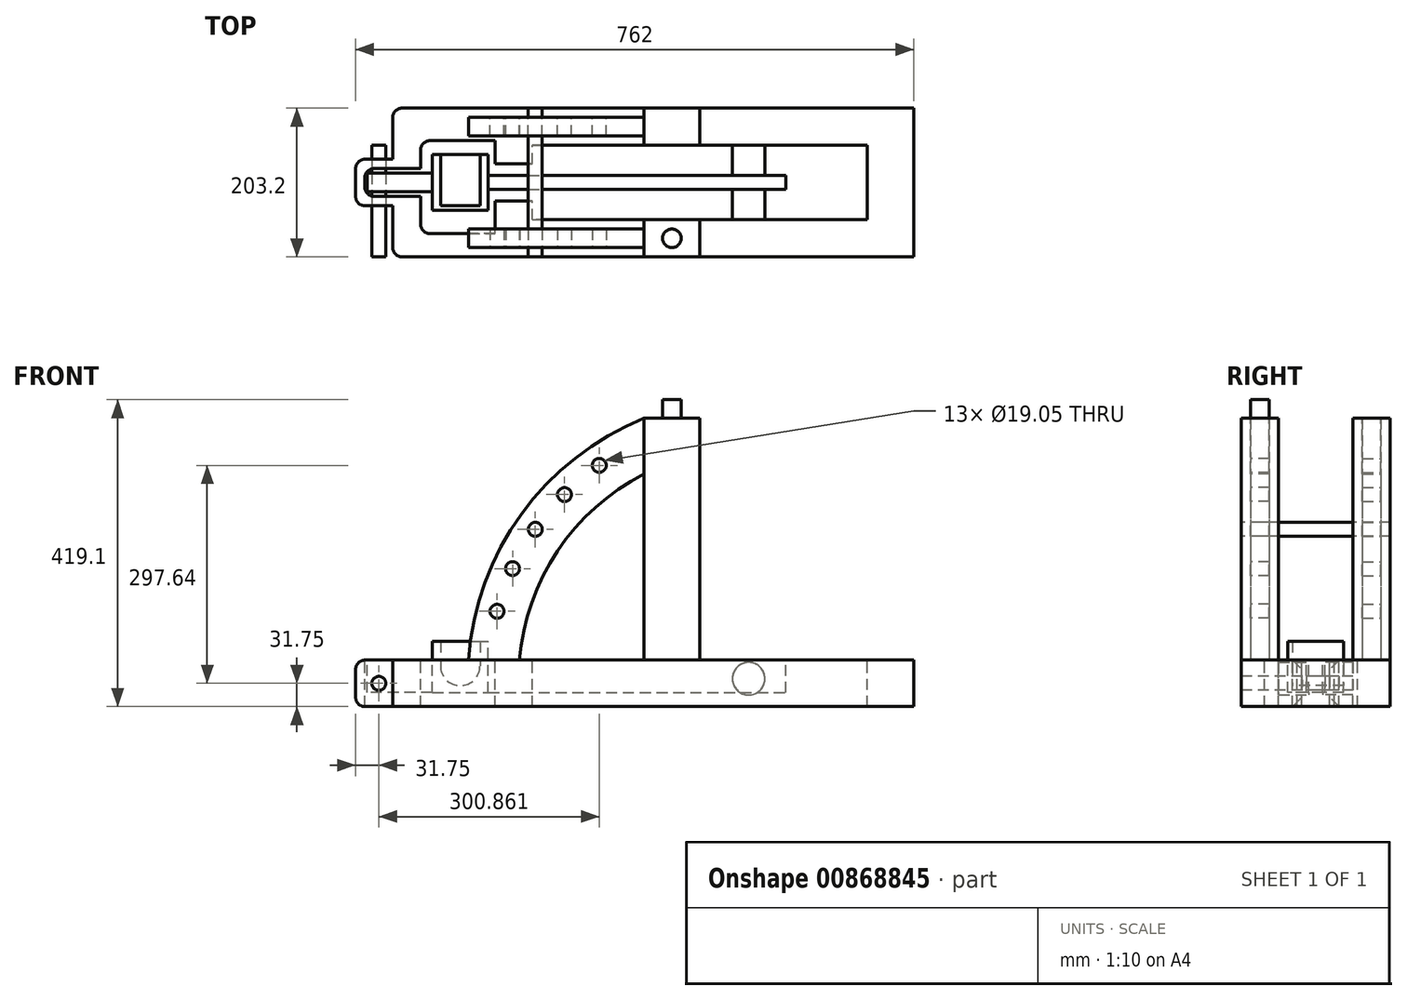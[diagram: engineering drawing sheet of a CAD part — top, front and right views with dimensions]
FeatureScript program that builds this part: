
annotation { "Feature Type Name" : "Feature", "Feature Type Description" : "" }
export const myFeature = defineFeature(function(context is Context, id is Id, definition is map)
    precondition{}
    {
        {
            var Q0;
            Q0=qCreatedBy(makeId("Top.planeOp"),FACE);
            var sketch = newSketch(context, id + "F0", { "sketchPlane" : qUnion([Q0])});
            skLineSegment(sketch, "E0", {"start": v(-330.2, 203.2) * mm, "end": v(330.2, 203.2) * mm});
            skLineSegment(sketch, "E1", {"start": v(-330.2, 0) * mm, "end": v(330.2, 0) * mm});
            skLineSegment(sketch, "E2", {"start": v(330.2, 203.2) * mm, "end": v(330.2, 0) * mm});
            skLineSegment(sketch, "E3", {"start": v(-330.2, 203.2) * mm, "end": v(-381, 203.2) * mm});
            skLineSegment(sketch, "E4", {"start": v(-381, 203.2) * mm, "end": v(-381, 133.35) * mm});
            skLineSegment(sketch, "E5", {"start": v(-381, 133.35) * mm, "end": v(-431.8, 133.35) * mm});
            skLineSegment(sketch, "E6", {"start": v(-431.8, 133.35) * mm, "end": v(-431.8, 69.85) * mm});
            skLineSegment(sketch, "E7", {"start": v(-431.8, 69.85) * mm, "end": v(-381, 69.85) * mm});
            skLineSegment(sketch, "E8", {"start": v(-381, 69.85) * mm, "end": v(-381, 0) * mm});
            skLineSegment(sketch, "E9", {"start": v(-381, 0) * mm, "end": v(-330.2, 0) * mm});
            skLineSegment(sketch, "E10", {"start": v(0, 203.2) * mm, "end": v(0, 0) * mm, "construction": true});
            skSolve(sketch);
        }
        {
            var Q0;
            Q0 = qSketchRegion(id + "F0", true);
            extrude(context, id + "F1", {"entities" : qUnion([Q0]), "oppositeDirection" : true, "depth" : 63.5 * mm, "offsetDistance" : 25.4 * mm});
        }
        {
            var Q0;
            Q0=makeQuery(id+"F1.opExtrude","CAP_FACE",FACE,{"disambiguationData":[OSD([sQuery(id+"F0.wireOp",EDGE,"E0"),sQuery(id+"F0.wireOp",EDGE,"E1"),sQuery(id+"F0.wireOp",EDGE,"E2"),sQuery(id+"F0.wireOp",EDGE,"E3"),sQuery(id+"F0.wireOp",EDGE,"E4"),sQuery(id+"F0.wireOp",EDGE,"E5"),sQuery(id+"F0.wireOp",EDGE,"E6"),sQuery(id+"F0.wireOp",EDGE,"E7"),sQuery(id+"F0.wireOp",EDGE,"E8"),sQuery(id+"F0.wireOp",EDGE,"E9")])],"isStart":true});
            var sketch = newSketch(context, id + "F2", { "sketchPlane" : qUnion([Q0])});
            skLineSegment(sketch, "E11", {"start": v(-342.9, 158.75) * mm, "end": v(-342.9, 120.65) * mm});
            skLineSegment(sketch, "E12", {"start": v(-342.9, 120.65) * mm, "end": v(-419.1, 120.65) * mm});
            skLineSegment(sketch, "E13", {"start": v(-419.1, 120.65) * mm, "end": v(-419.1, 82.55) * mm});
            skLineSegment(sketch, "E14", {"start": v(-419.1, 82.55) * mm, "end": v(-342.9, 82.55) * mm});
            skLineSegment(sketch, "E15", {"start": v(-342.9, 82.55) * mm, "end": v(-342.9, 31.75) * mm});
            skLineSegment(sketch, "E16", {"start": v(-342.9, 31.75) * mm, "end": v(-241.3, 31.75) * mm});
            skLineSegment(sketch, "E17", {"start": v(-241.3, 31.75) * mm, "end": v(-241.3, 76.2) * mm});
            skLineSegment(sketch, "E18", {"start": v(-241.3, 76.2) * mm, "end": v(-190.5, 76.2) * mm});
            skLineSegment(sketch, "E19", {"start": v(-190.5, 76.2) * mm, "end": v(-190.5, 50.8) * mm});
            skLineSegment(sketch, "E20", {"start": v(-190.5, 50.8) * mm, "end": v(266.7, 50.8) * mm});
            skLineSegment(sketch, "E21", {"start": v(266.7, 50.8) * mm, "end": v(266.7, 152.4) * mm});
            skLineSegment(sketch, "E22", {"start": v(266.7, 152.4) * mm, "end": v(-190.5, 152.4) * mm});
            skLineSegment(sketch, "E23", {"start": v(-190.5, 152.4) * mm, "end": v(-190.5, 127) * mm});
            skLineSegment(sketch, "E24", {"start": v(-190.5, 127) * mm, "end": v(-241.3, 127) * mm});
            skLineSegment(sketch, "E25", {"start": v(-241.3, 127) * mm, "end": v(-241.3, 158.75) * mm});
            skLineSegment(sketch, "E26", {"start": v(-241.3, 158.75) * mm, "end": v(-342.9, 158.75) * mm});
            skSolve(sketch);
        }
        {
            var Q0;
            Q0 = qSketchRegion(id + "F2", true);
            var Q1;
            Q1=makeQuery(id+"F1.opExtrude","CAP_FACE",FACE,{"disambiguationData":[OSD([sQuery(id+"F0.wireOp",EDGE,"E0"),sQuery(id+"F0.wireOp",EDGE,"E1"),sQuery(id+"F0.wireOp",EDGE,"E2"),sQuery(id+"F0.wireOp",EDGE,"E3"),sQuery(id+"F0.wireOp",EDGE,"E4"),sQuery(id+"F0.wireOp",EDGE,"E5"),sQuery(id+"F0.wireOp",EDGE,"E6"),sQuery(id+"F0.wireOp",EDGE,"E7"),sQuery(id+"F0.wireOp",EDGE,"E8"),sQuery(id+"F0.wireOp",EDGE,"E9")])],"isStart":false});
            extrude(context, id + "F3", {"entities" : qUnion([Q0]), "operationType" : NewBodyOperationType.REMOVE, "endBound" : BoundingType.UP_TO_SURFACE, "oppositeDirection" : true, "depth" : 25.4 * mm, "endBoundEntityFace" : qUnion([Q1]), "offsetDistance" : 25.4 * mm});
        }
        {
            var Q0;
            Q0=makeQuery(id+"F3.boolean.opBoolean","COPY",EDGE,{"derivedFrom":makeQuery(id+"F3.opExtrude","SWEPT_EDGE",EDGE,{"disambiguationData":[OSD([sQuery(id+"F2.wireOp",EDGE,"E12"),sQuery(id+"F2.wireOp",EDGE,"E13")])]})});
            var Q1;
            Q1=makeQuery(id+"F3.boolean.opBoolean","COPY",EDGE,{"derivedFrom":makeQuery(id+"F3.opExtrude","SWEPT_EDGE",EDGE,{"disambiguationData":[OSD([sQuery(id+"F2.wireOp",EDGE,"E13"),sQuery(id+"F2.wireOp",EDGE,"E14")])]})});
            fillet(context, id + "F4", {"entities" : qUnion([Q0, Q1]), "radius" : 12.7 * mm, "tangentPropagation" : true, "allowEdgeOverflow" : false});
        }
        {
            var Q0;
            Q0=makeQuery(id+"F3.boolean.opBoolean","COPY",EDGE,{"derivedFrom":makeQuery(id+"F3.opExtrude","SWEPT_EDGE",EDGE,{"disambiguationData":[OSD([sQuery(id+"F2.wireOp",EDGE,"E11"),sQuery(id+"F2.wireOp",EDGE,"E26")])]})});
            var Q1;
            Q1=makeQuery(id+"F3.boolean.opBoolean","COPY",EDGE,{"derivedFrom":makeQuery(id+"F3.opExtrude","SWEPT_EDGE",EDGE,{"disambiguationData":[OSD([sQuery(id+"F2.wireOp",EDGE,"E15"),sQuery(id+"F2.wireOp",EDGE,"E16")])]})});
            var Q2;
            Q2=makeQuery(id+"F1.opExtrude","CAP_EDGE",EDGE,{"disambiguationData":[OSD([sQuery(id+"F0.wireOp",EDGE,"E6")])],"isStart":true});
            var Q3;
            Q3=makeQuery(id+"F1.opExtrude","SWEPT_EDGE",EDGE,{"disambiguationData":[OSD([sQuery(id+"F0.wireOp",EDGE,"E8"),sQuery(id+"F0.wireOp",EDGE,"E9")])]});
            var Q4;
            Q4=makeQuery(id+"F1.opExtrude","SWEPT_EDGE",EDGE,{"disambiguationData":[OSD([sQuery(id+"F0.wireOp",EDGE,"E3"),sQuery(id+"F0.wireOp",EDGE,"E4")])]});
            var Q5;
            Q5=makeQuery(id+"F1.opExtrude","SWEPT_FACE",FACE,{"disambiguationData":[OSD([sQuery(id+"F0.wireOp",EDGE,"E6")])]});
            fillet(context, id + "F5", {"entities" : qUnion([Q0, Q1, Q2, Q3, Q4, Q5]), "radius" : 12.7 * mm, "tangentPropagation" : true, "allowEdgeOverflow" : false});
        }
        {
            var Q0;
            Q0=qCreatedBy(makeId("Front.planeOp"),FACE);
            var sketch = newSketch(context, id + "F6", { "sketchPlane" : qUnion([Q0])});
            skLineSegment(sketch, "E27", {"start": v(-38.1, 0) * mm, "end": v(38.1, 0) * mm});
            skLineSegment(sketch, "E28", {"start": v(38.1, 0) * mm, "end": v(38.1, 330.2) * mm});
            skLineSegment(sketch, "E29", {"start": v(38.1, 330.2) * mm, "end": v(-38.1, 330.2) * mm});
            skLineSegment(sketch, "E30", {"start": v(-38.1, 330.2) * mm, "end": v(-38.1, 0) * mm});
            skSolve(sketch);
        }
        {
            var Q0;
            Q0=makeQuery(id+"F3.boolean.opBoolean","COPY",FACE,{"derivedFrom":makeQuery(id+"F3.opExtrude","SWEPT_FACE",FACE,{"disambiguationData":[OSD([sQuery(id+"F2.wireOp",EDGE,"E20")])]})});
            cPlane(context, id + "F7", {"entities" : qUnion([Q0]), "cplaneType" : CPlaneType.OFFSET, "offset" : 50.8 * mm, "width" : 152.4 * mm, "height" : 152.4 * mm});
        }
        {
            var Q0;
            Q0 = qSketchRegion(id + "F6", true);
            var Q1;
            Q1=makeQuery(id+"F3.boolean.opBoolean","COPY",FACE,{"derivedFrom":makeQuery(id+"F3.opExtrude","SWEPT_FACE",FACE,{"disambiguationData":[OSD([sQuery(id+"F2.wireOp",EDGE,"E20")])]})});
            extrude(context, id + "F8", {"entities" : qUnion([Q0]), "endBound" : BoundingType.UP_TO_SURFACE, "oppositeDirection" : true, "depth" : 25.4 * mm, "endBoundEntityFace" : qUnion([Q1]), "offsetDistance" : 25.4 * mm});
        }
        {
            var Q0;
            Q0=makeQuery(id+"F8.opExtrude","SWEPT_BODY",BODY,{"disambiguationData":[OSD([sQuery(id+"F6.wireOp",EDGE,"E27"),sQuery(id+"F6.wireOp",EDGE,"E28"),sQuery(id+"F6.wireOp",EDGE,"E29"),sQuery(id+"F6.wireOp",EDGE,"E30")])]});
            var Q1;
            Q1=qCreatedBy(id+"F7.planeOp",FACE);
            mirror(context, id + "F9", {"entities" : qUnion([Q0]), "mirrorPlane" : qUnion([Q1])});
        }
        {
            var Q0;
            Q0=makeQuery(id+"F3.boolean.opBoolean","COPY",FACE,{"derivedFrom":makeQuery(id+"F3.opExtrude","SWEPT_FACE",FACE,{"disambiguationData":[OSD([sQuery(id+"F2.wireOp",EDGE,"E22")])]})});
            var sketch = newSketch(context, id + "F10", { "sketchPlane" : qUnion([Q0])});
            skCircle(sketch, "E31", {"center": v(104.77, -25.4) * mm, "radius": 15.88 * mm});
            skLineSegment(sketch, "E32", {"start": v(266.7, -25.4) * mm, "end": v(-95.08, -25.4) * mm, "construction": true});
            skSolve(sketch);
        }
        {
            var Q0;
            Q0 = qSketchRegion(id + "F10", true);
            extrude(context, id + "F11", {"entities" : qUnion([Q0]), "operationType" : NewBodyOperationType.REMOVE, "oppositeDirection" : true, "depth" : 25.4 * mm, "offsetDistance" : 25.4 * mm});
        }
        {
            var Q0;
            Q0=makeQuery(id+"F3.boolean.opBoolean","COPY",FACE,{"derivedFrom":makeQuery(id+"F3.opExtrude","SWEPT_FACE",FACE,{"disambiguationData":[OSD([sQuery(id+"F2.wireOp",EDGE,"E20")])]})});
            var sketch = newSketch(context, id + "F12", { "sketchPlane" : qUnion([Q0])});
            skCircle(sketch, "E33.0", {"center": v(-104.77, -25.4) * mm, "radius": 15.88 * mm});
            skSolve(sketch);
        }
        {
            var Q0;
            Q0 = qSketchRegion(id + "F12", true);
            extrude(context, id + "F13", {"entities" : qUnion([Q0]), "operationType" : NewBodyOperationType.REMOVE, "oppositeDirection" : true, "depth" : 25.4 * mm, "offsetDistance" : 25.4 * mm});
        }
        {
            var Q0;
            Q0=qCreatedBy(makeId("Top.planeOp"),FACE);
            var sketch = newSketch(context, id + "F14", { "sketchPlane" : qUnion([Q0])});
            skLineSegment(sketch, "E34.bottom", {"start": v(-327.03, 139.7) * mm, "end": v(-250.83, 139.7) * mm});
            skLineSegment(sketch, "E34.top", {"start": v(-327.03, 63.5) * mm, "end": v(-250.83, 63.5) * mm});
            skLineSegment(sketch, "E34.left", {"start": v(-327.03, 139.7) * mm, "end": v(-327.03, 63.5) * mm});
            skLineSegment(sketch, "E34.right", {"start": v(-250.83, 139.7) * mm, "end": v(-250.83, 63.5) * mm});
            skLineSegment(sketch, "E35.bottom", {"start": v(-327.03, 88.9) * mm, "end": v(-415.93, 88.9) * mm});
            skLineSegment(sketch, "E35.top", {"start": v(-327.03, 114.3) * mm, "end": v(-415.93, 114.3) * mm});
            skLineSegment(sketch, "E35.left", {"start": v(-327.03, 114.3) * mm, "end": v(-327.03, 88.9) * mm});
            skLineSegment(sketch, "E35.right", {"start": v(-415.93, 114.3) * mm, "end": v(-415.93, 88.9) * mm});
            skLineSegment(sketch, "E36.bottom", {"start": v(-250.83, 111.12) * mm, "end": v(155.57, 111.12) * mm});
            skLineSegment(sketch, "E36.top", {"start": v(-250.83, 92.08) * mm, "end": v(155.57, 92.08) * mm});
            skLineSegment(sketch, "E36.left", {"start": v(-250.83, 111.12) * mm, "end": v(-250.83, 92.07) * mm});
            skLineSegment(sketch, "E36.right", {"start": v(155.58, 111.12) * mm, "end": v(155.58, 92.08) * mm});
            skLineSegment(sketch, "E37.bottom", {"start": v(-57.57, 111.12) * mm, "end": v(-35.47, 111.12) * mm});
            skLineSegment(sketch, "E38", {"start": v(155.58, 101.6) * mm, "end": v(-122.44, 101.6) * mm, "construction": true});
            skPoint(sketch, "E39", {"position": v(-250.83, 101.6) * mm});
            skLineSegment(sketch, "E40", {"start": v(-250.83, 101.6) * mm, "end": v(-327.03, 101.6) * mm, "construction": true});
            skPoint(sketch, "E41", {"position": v(-327.03, 101.6) * mm});
            skSolve(sketch);
        }
        {
            var Q0;
            Q0 = qSketchRegion(id + "F14", true);
            extrude(context, id + "F15", {"entities" : qUnion([Q0]), "oppositeDirection" : true, "depth" : 44.45 * mm, "offsetDistance" : 25.4 * mm});
        }
        {
            var Q0;
            Q0=makeQuery(id+"F15.opExtrude","CAP_FACE",FACE,{"disambiguationData":[OSD([sQuery(id+"F14.wireOp",EDGE,"E34.bottom"),sQuery(id+"F14.wireOp",EDGE,"E34.top"),sQuery(id+"F14.wireOp",EDGE,"E34.left"),sQuery(id+"F14.wireOp",EDGE,"E34.right"),sQuery(id+"F14.wireOp",EDGE,"E35.bottom"),sQuery(id+"F14.wireOp",EDGE,"E35.top"),sQuery(id+"F14.wireOp",EDGE,"E35.right"),sQuery(id+"F14.wireOp",EDGE,"E36.bottom"),sQuery(id+"F14.wireOp",EDGE,"E36.top"),sQuery(id+"F14.wireOp",EDGE,"E36.right"),sQuery(id+"F14.wireOp",EDGE,"E37.bottom")])],"isStart":true});
            var sketch = newSketch(context, id + "F16", { "sketchPlane" : qUnion([Q0])});
            skLineSegment(sketch, "E42.bottom", {"start": v(-320.68, 133.35) * mm, "end": v(-257.18, 133.35) * mm});
            skLineSegment(sketch, "E42.top", {"start": v(-320.68, 69.85) * mm, "end": v(-257.18, 69.85) * mm});
            skLineSegment(sketch, "E42.left", {"start": v(-320.68, 133.35) * mm, "end": v(-320.68, 69.85) * mm});
            skLineSegment(sketch, "E42.right", {"start": v(-257.18, 133.35) * mm, "end": v(-257.18, 69.85) * mm});
            skSolve(sketch);
        }
        {
            var Q0;
            Q0 = qSketchRegion(id + "F16", true);
            extrude(context, id + "F17", {"entities" : qUnion([Q0]), "operationType" : NewBodyOperationType.REMOVE, "oppositeDirection" : true, "depth" : 25.4 * mm, "offsetDistance" : 25.4 * mm});
        }
        {
            var Q0;
            Q0=makeQuery(id+"F1.opExtrude","SWEPT_FACE",FACE,{"disambiguationData":[OSD([sQuery(id+"F0.wireOp",EDGE,"E7")])]});
            var sketch = newSketch(context, id + "F18", { "sketchPlane" : qUnion([Q0])});
            skCircle(sketch, "E43", {"center": v(-400.05, -31.75) * mm, "radius": 9.53 * mm});
            skLineSegment(sketch, "E44", {"start": v(-400.05, 0) * mm, "end": v(-400.05, -63.5) * mm, "construction": true});
            skSolve(sketch);
        }
        {
            var Q0;
            {var subQ0=sQuery(id+"F18.wireOp",EDGE,"E43");var subQ1=sQuery(id+"F0.wireOp",EDGE,"E7");var subQ2=makeQuery(id+"F5.opFillet","BLEND_EDGE",EDGE,{"blendedFrom":[makeQuery(id+"F1.opExtrude","SWEPT_EDGE",EDGE,{"disambiguationData":[OSD([sQuery(id+"F0.wireOp",EDGE,"E6"),subQ1])]}),makeQuery(id+"F1.opExtrude","SWEPT_FACE",FACE,{"disambiguationData":[OSD([subQ1])]})],"blendedInto":[makeQuery(id+"F1.opExtrude","SWEPT_FACE",FACE,{"disambiguationData":[OSD([subQ1])]})]});var subQ3=makeQuery(id+"F18.imprint","INTERSECT",VERTEX,{"disambiguationData":[OD(0.0)],"derivedFrom":[subQ2,subQ0]});Q0=makeQuery(id+"F18.imprint","IMPRINT",FACE,{"disambiguationData":[TD([[makeQuery(id+"F18.imprint","IMPRINT",EDGE,{"disambiguationData":[TD([[subQ3,-1.0]])],"derivedFrom":subQ0}),1.0]])]});}
            var Q1;
            Q1=makeQuery(id+"F1.opExtrude","SWEPT_FACE",FACE,{"disambiguationData":[OSD([sQuery(id+"F0.wireOp",EDGE,"E5")])]});
            extrude(context, id + "F19", {"entities" : qUnion([Q0]), "operationType" : NewBodyOperationType.REMOVE, "endBound" : BoundingType.UP_TO_SURFACE, "oppositeDirection" : true, "depth" : 25.4 * mm, "endBoundEntityFace" : qUnion([Q1]), "offsetDistance" : 25.4 * mm});
        }
        {
            var Q0;
            Q0=makeQuery(id+"F15.opExtrude","SWEPT_FACE",FACE,{"disambiguationData":[OSD([sQuery(id+"F14.wireOp",EDGE,"E35.bottom")])]});
            var sketch = newSketch(context, id + "F20", { "sketchPlane" : qUnion([Q0])});
            skCircle(sketch, "E45.0", {"center": v(-400.05, -31.75) * mm, "radius": 9.53 * mm});
            skCircle(sketch, "E46.0", {"center": v(104.77, -25.4) * mm, "radius": 15.88 * mm});
            skSolve(sketch);
        }
        {
            var Q0;
            Q0 = qSketchRegion(id + "F20", true);
            var Q1;
            Q1=makeQuery(id+"F15.opExtrude","SWEPT_FACE",FACE,{"disambiguationData":[OSD([sQuery(id+"F14.wireOp",EDGE,"E35.top")])]});
            extrude(context, id + "F21", {"entities" : qUnion([Q0]), "operationType" : NewBodyOperationType.REMOVE, "endBound" : BoundingType.UP_TO_SURFACE, "oppositeDirection" : true, "depth" : 25.4 * mm, "endBoundEntityFace" : qUnion([Q1]), "offsetDistance" : 25.4 * mm});
        }
        {
            var Q0;
            Q0=makeQuery(id+"F9.opPattern","COPY",FACE,{"derivedFrom":makeQuery(id+"F8.opExtrude","CAP_FACE",FACE,{"disambiguationData":[OSD([sQuery(id+"F6.wireOp",EDGE,"E27"),sQuery(id+"F6.wireOp",EDGE,"E28"),sQuery(id+"F6.wireOp",EDGE,"E29"),sQuery(id+"F6.wireOp",EDGE,"E30")])],"isStart":false}),"instanceName":"1"});
            var sketch = newSketch(context, id + "F22", { "sketchPlane" : qUnion([Q0])});
            skCircle(sketch, "E47", {"center": v(104.77, -25.4) * mm, "radius": 355.6 * mm, "construction": true});
            skLineSegment(sketch, "E48", {"start": v(104.77, -25.4) * mm, "end": v(-146.67, 226.05) * mm, "construction": true});
            skLineSegment(sketch, "E49", {"start": v(104.77, -25.4) * mm, "end": v(-99.19, 265.9) * mm, "construction": true});
            skLineSegment(sketch, "E50", {"start": v(-186.52, 178.56) * mm, "end": v(104.78, -25.4) * mm, "construction": true});
            skLineSegment(sketch, "E51", {"start": v(-217.5, 124.88) * mm, "end": v(104.77, -25.4) * mm, "construction": true});
            skLineSegment(sketch, "E52", {"start": v(-238.7, 66.64) * mm, "end": v(104.78, -25.4) * mm, "construction": true});
            skArc(sketch, "E53", {"start": v(-38.1, 330.2) * mm, "mid": v(-205.44, 199.61) * mm, "end": v(-277.61, 0) * mm});
            skArc(sketch, "E54", {"start": v(-38.1, 254) * mm, "mid": v(-156.06, 149.08) * mm, "end": v(-208, 0) * mm});
            skLineSegment(sketch, "E55", {"start": v(-38.1, 330.2) * mm, "end": v(-38.1, 254) * mm});
            skLineSegment(sketch, "E56", {"start": v(-208, 0) * mm, "end": v(-277.61, 0) * mm});
            skCircle(sketch, "E57", {"center": v(-99.19, 265.9) * mm, "radius": 9.53 * mm});
            skCircle(sketch, "E58", {"center": v(-146.67, 226.05) * mm, "radius": 9.53 * mm});
            skCircle(sketch, "E59", {"center": v(-186.52, 178.56) * mm, "radius": 9.53 * mm});
            skCircle(sketch, "E60", {"center": v(-217.5, 124.88) * mm, "radius": 9.53 * mm});
            skCircle(sketch, "E61", {"center": v(-238.7, 66.64) * mm, "radius": 9.53 * mm});
            skSolve(sketch);
        }
        {
            var Q0;
            Q0 = qSketchRegion(id + "F22", true);
            extrude(context, id + "F23", {"entities" : qUnion([Q0]), "depth" : 25.4 * mm, "offsetDistance" : 25.4 * mm});
        }
        {
            var Q0;
            Q0=makeQuery(id+"F23.opExtrude","SWEPT_BODY",BODY,{"disambiguationData":[OSD([sQuery(id+"F22.wireOp",EDGE,"E53"),sQuery(id+"F22.wireOp",EDGE,"E54"),sQuery(id+"F22.wireOp",EDGE,"E55"),sQuery(id+"F22.wireOp",EDGE,"E56")])]});
            var Q1;
            Q1=makeQuery(id+"F3.boolean.opBoolean","COPY",FACE,{"derivedFrom":makeQuery(id+"F3.opExtrude","SWEPT_FACE",FACE,{"disambiguationData":[OSD([sQuery(id+"F2.wireOp",EDGE,"E22")])]})});
            transform(context, id + "F24", {"entities" : qUnion([Q0]), "transformType" : TransformType.TRANSLATION_DISTANCE, "transformDirection" : qUnion([Q1]), "distance" : 38.1 * mm, "oppositeDirection" : true, "makeCopy" : false});
        }
        {
            var Q0;
            Q0=makeQuery(id+"F23.opExtrude","SWEPT_BODY",BODY,{"disambiguationData":[OSD([sQuery(id+"F22.wireOp",EDGE,"E53"),sQuery(id+"F22.wireOp",EDGE,"E54"),sQuery(id+"F22.wireOp",EDGE,"E55"),sQuery(id+"F22.wireOp",EDGE,"E56")])]});
            var Q1;
            Q1=qCreatedBy(id+"F7.planeOp",FACE);
            mirror(context, id + "F25", {"entities" : qUnion([Q0]), "mirrorPlane" : qUnion([Q1])});
        }
        {
            var Q0;
            Q0=makeQuery(id+"F11.boolean.opBoolean","COPY",FACE,{"derivedFrom":makeQuery(id+"F11.opExtrude","CAP_FACE",FACE,{"disambiguationData":[OSD([sQuery(id+"F10.wireOp",EDGE,"E31")])],"isStart":false})});
            var sketch = newSketch(context, id + "F26", { "sketchPlane" : qUnion([Q0])});
            skCircle(sketch, "E62.0", {"center": v(104.77, -25.4) * mm, "radius": 15.88 * mm});
            skSolve(sketch);
        }
        {
            var Q0;
            Q0 = qSketchRegion(id + "F26", true);
            var Q1;
            Q1=makeQuery(id+"F13.boolean.opBoolean","COPY",FACE,{"derivedFrom":makeQuery(id+"F13.opExtrude","CAP_FACE",FACE,{"disambiguationData":[OSD([sQuery(id+"F12.wireOp",EDGE,"E33.0")])],"isStart":false})});
            extrude(context, id + "F27", {"entities" : qUnion([Q0]), "endBound" : BoundingType.UP_TO_SURFACE, "depth" : 25.4 * mm, "endBoundEntityFace" : qUnion([Q1]), "offsetDistance" : 25.4 * mm});
        }
        {
            var Q0;
            Q0=makeQuery(id+"F15.opExtrude","CAP_FACE",FACE,{"disambiguationData":[OSD([sQuery(id+"F14.wireOp",EDGE,"E34.bottom"),sQuery(id+"F14.wireOp",EDGE,"E34.top"),sQuery(id+"F14.wireOp",EDGE,"E34.left"),sQuery(id+"F14.wireOp",EDGE,"E34.right"),sQuery(id+"F14.wireOp",EDGE,"E35.bottom"),sQuery(id+"F14.wireOp",EDGE,"E35.top"),sQuery(id+"F14.wireOp",EDGE,"E35.right"),sQuery(id+"F14.wireOp",EDGE,"E36.bottom"),sQuery(id+"F14.wireOp",EDGE,"E36.top"),sQuery(id+"F14.wireOp",EDGE,"E36.right"),sQuery(id+"F14.wireOp",EDGE,"E37.bottom")])],"isStart":true});
            var sketch = newSketch(context, id + "F28", { "sketchPlane" : qUnion([Q0])});
            skLineSegment(sketch, "E63.bottom", {"start": v(-327.03, 139.7) * mm, "end": v(-250.83, 139.7) * mm});
            skLineSegment(sketch, "E63.top", {"start": v(-327.03, 63.5) * mm, "end": v(-250.83, 63.5) * mm});
            skLineSegment(sketch, "E63.left", {"start": v(-327.03, 139.7) * mm, "end": v(-327.03, 63.5) * mm});
            skLineSegment(sketch, "E63.right", {"start": v(-250.83, 139.7) * mm, "end": v(-250.83, 63.5) * mm});
            skSolve(sketch);
        }
        {
            var Q0;
            Q0 = qSketchRegion(id + "F28", true);
            var Q1;
            Q1=makeQuery(id+"F17.boolean.opBoolean","COPY",FACE,{"derivedFrom":makeQuery(id+"F17.opExtrude","CAP_FACE",FACE,{"disambiguationData":[OSD([sQuery(id+"F16.wireOp",EDGE,"E42.bottom"),sQuery(id+"F16.wireOp",EDGE,"E42.top"),sQuery(id+"F16.wireOp",EDGE,"E42.left"),sQuery(id+"F16.wireOp",EDGE,"E42.right")])],"isStart":false})});
            extrude(context, id + "F29", {"entities" : qUnion([Q0]), "operationType" : NewBodyOperationType.ADD, "endBound" : BoundingType.UP_TO_SURFACE, "oppositeDirection" : true, "depth" : 25.4 * mm, "endBoundEntityFace" : qUnion([Q1]), "offsetDistance" : 25.4 * mm});
        }
        {
            var Q0;
            Q0=makeQuery(id+"F29.boolean.opBoolean","MERGE",FACE,{"derivedFrom":[makeQuery(id+"F15.opExtrude","CAP_FACE",FACE,{"disambiguationData":[OSD([sQuery(id+"F14.wireOp",EDGE,"E34.bottom"),sQuery(id+"F14.wireOp",EDGE,"E34.top"),sQuery(id+"F14.wireOp",EDGE,"E34.left"),sQuery(id+"F14.wireOp",EDGE,"E34.right"),sQuery(id+"F14.wireOp",EDGE,"E35.bottom"),sQuery(id+"F14.wireOp",EDGE,"E35.top"),sQuery(id+"F14.wireOp",EDGE,"E35.right"),sQuery(id+"F14.wireOp",EDGE,"E36.bottom"),sQuery(id+"F14.wireOp",EDGE,"E36.top"),sQuery(id+"F14.wireOp",EDGE,"E36.right"),sQuery(id+"F14.wireOp",EDGE,"E37.bottom")])],"isStart":true}),makeQuery(id+"F29.opExtrude","CAP_FACE",FACE,{"disambiguationData":[OSD([sQuery(id+"F28.wireOp",EDGE,"E63.bottom"),sQuery(id+"F28.wireOp",EDGE,"E63.top"),sQuery(id+"F28.wireOp",EDGE,"E63.left"),sQuery(id+"F28.wireOp",EDGE,"E63.right")])],"isStart":true})]});
            var sketch = newSketch(context, id + "F30", { "sketchPlane" : qUnion([Q0])});
            skLineSegment(sketch, "E64.bottom", {"start": v(-327.03, 139.7) * mm, "end": v(-250.83, 139.7) * mm});
            skLineSegment(sketch, "E64.top", {"start": v(-327.03, 63.5) * mm, "end": v(-250.83, 63.5) * mm});
            skLineSegment(sketch, "E64.left", {"start": v(-327.03, 139.7) * mm, "end": v(-327.03, 63.5) * mm});
            skLineSegment(sketch, "E64.right", {"start": v(-250.83, 139.7) * mm, "end": v(-250.83, 63.5) * mm});
            skSolve(sketch);
        }
        {
            var Q0;
            Q0 = qSketchRegion(id + "F30", true);
            extrude(context, id + "F31", {"entities" : qUnion([Q0]), "operationType" : NewBodyOperationType.ADD, "depth" : 25.4 * mm, "offsetDistance" : 25.4 * mm});
        }
        {
            var Q0;
            Q0=makeQuery(id+"F31.boolean.opBoolean","MERGE",FACE,{"derivedFrom":[makeQuery(id+"F15.opExtrude","SWEPT_FACE",FACE,{"disambiguationData":[OSD([sQuery(id+"F14.wireOp",EDGE,"E34.top")])]}),makeQuery(id+"F31.opExtrude","SWEPT_FACE",FACE,{"disambiguationData":[OSD([sQuery(id+"F30.wireOp",EDGE,"E64.top")])]})]});
            var sketch = newSketch(context, id + "F32", { "sketchPlane" : qUnion([Q0])});
            skLineSegment(sketch, "E65", {"start": v(-288.93, 25.4) * mm, "end": v(-288.93, -7.94) * mm, "construction": true});
            skArc(sketch, "E66", {"start": v(-315.91, -7.94) * mm, "mid": v(-288.93, -34.92) * mm, "end": v(-261.94, -7.94) * mm});
            skLineSegment(sketch, "E67", {"start": v(-315.91, -7.94) * mm, "end": v(-261.94, -7.94) * mm, "construction": true});
            skLineSegment(sketch, "E68", {"start": v(-315.91, -7.94) * mm, "end": v(-315.91, 25.4) * mm});
            skLineSegment(sketch, "E69", {"start": v(-261.94, -7.94) * mm, "end": v(-261.94, 25.4) * mm});
            skLineSegment(sketch, "E70", {"start": v(-261.94, 25.4) * mm, "end": v(-315.91, 25.4) * mm});
            skLineSegment(sketch, "E71", {"start": v(-288.93, -34.93) * mm, "end": v(-288.93, -44.45) * mm, "construction": true});
            skSolve(sketch);
        }
        {
            var Q0;
            Q0 = qSketchRegion(id + "F32", true);
            var Q1;
            Q1=makeQuery(id+"F31.boolean.opBoolean","MERGE",FACE,{"derivedFrom":[makeQuery(id+"F15.opExtrude","SWEPT_FACE",FACE,{"disambiguationData":[OSD([sQuery(id+"F14.wireOp",EDGE,"E34.bottom")])]}),makeQuery(id+"F31.opExtrude","SWEPT_FACE",FACE,{"disambiguationData":[OSD([sQuery(id+"F30.wireOp",EDGE,"E64.bottom")])]})]});
            extrude(context, id + "F33", {"entities" : qUnion([Q0]), "operationType" : NewBodyOperationType.REMOVE, "endBound" : BoundingType.UP_TO_SURFACE, "oppositeDirection" : true, "depth" : 25.4 * mm, "endBoundEntityFace" : qUnion([Q1]), "offsetDistance" : 25.4 * mm});
        }
        {
            var Q0;
            Q0=makeQuery(id+"F31.boolean.opBoolean","MERGE",FACE,{"derivedFrom":[makeQuery(id+"F15.opExtrude","SWEPT_FACE",FACE,{"disambiguationData":[OSD([sQuery(id+"F14.wireOp",EDGE,"E34.top")])]}),makeQuery(id+"F31.opExtrude","SWEPT_FACE",FACE,{"disambiguationData":[OSD([sQuery(id+"F30.wireOp",EDGE,"E64.top")])]})]});
            var sketch = newSketch(context, id + "F34", { "sketchPlane" : qUnion([Q0])});
            skLineSegment(sketch, "E72.bottom", {"start": v(-250.83, -44.45) * mm, "end": v(-327.03, -44.45) * mm});
            skLineSegment(sketch, "E72.top", {"start": v(-250.83, 25.4) * mm, "end": v(-327.03, 25.4) * mm});
            skLineSegment(sketch, "E72.left", {"start": v(-250.83, -44.45) * mm, "end": v(-250.83, 25.4) * mm});
            skLineSegment(sketch, "E72.right", {"start": v(-327.03, -44.45) * mm, "end": v(-327.03, 25.4) * mm});
            skSolve(sketch);
        }
        {
            var Q0;
            Q0 = qSketchRegion(id + "F34", true);
            extrude(context, id + "F35", {"entities" : qUnion([Q0]), "operationType" : NewBodyOperationType.ADD, "oppositeDirection" : true, "depth" : 6.35 * mm, "offsetDistance" : 25.4 * mm});
        }
        {
            var Q0;
            Q0=makeQuery(id+"F1.opExtrude","SWEPT_FACE",FACE,{"disambiguationData":[OSD([sQuery(id+"F0.wireOp",EDGE,"E1"),sQuery(id+"F0.wireOp",EDGE,"E9")])]});
            var sketch = newSketch(context, id + "F36", { "sketchPlane" : qUnion([Q0])});
            skCircle(sketch, "E73.0", {"center": v(-400.05, -31.75) * mm, "radius": 9.53 * mm});
            skSolve(sketch);
        }
        {
            var Q0;
            Q0=makeQuery(id+"F36.imprint","IMPRINT",FACE,{"disambiguationData":[TD([[makeQuery(id+"F36.imprint","IMPRINT",EDGE,{"derivedFrom":sQuery(id+"F36.wireOp",EDGE,"E73.0")}),1.0]])]});
            extrude(context, id + "F37", {"entities" : qUnion([Q0]), "oppositeDirection" : true, "depth" : 152.4 * mm, "offsetDistance" : 25.4 * mm});
        }
        {
            var Q0;
            Q0=makeQuery(id+"F8.opExtrude","CAP_FACE",FACE,{"disambiguationData":[OSD([sQuery(id+"F6.wireOp",EDGE,"E27"),sQuery(id+"F6.wireOp",EDGE,"E28"),sQuery(id+"F6.wireOp",EDGE,"E29"),sQuery(id+"F6.wireOp",EDGE,"E30")])],"isStart":true});
            var sketch = newSketch(context, id + "F38", { "sketchPlane" : qUnion([Q0])});
            skCircle(sketch, "E74.0", {"center": v(-186.52, 178.56) * mm, "radius": 9.53 * mm});
            skSolve(sketch);
        }
        {
            var Q0;
            Q0 = qSketchRegion(id + "F38", true);
            var Q1;
            Q1=makeQuery(id+"F9.opPattern","COPY",FACE,{"derivedFrom":makeQuery(id+"F8.opExtrude","CAP_FACE",FACE,{"disambiguationData":[OSD([sQuery(id+"F6.wireOp",EDGE,"E27"),sQuery(id+"F6.wireOp",EDGE,"E28"),sQuery(id+"F6.wireOp",EDGE,"E29"),sQuery(id+"F6.wireOp",EDGE,"E30")])],"isStart":true}),"instanceName":"1"});
            extrude(context, id + "F39", {"entities" : qUnion([Q0]), "endBound" : BoundingType.UP_TO_SURFACE, "oppositeDirection" : true, "depth" : 25.4 * mm, "endBoundEntityFace" : qUnion([Q1]), "offsetDistance" : 25.4 * mm});
        }
        {
            var Q0;
            Q0=makeQuery(id+"F8.opExtrude","SWEPT_FACE",FACE,{"disambiguationData":[OSD([sQuery(id+"F6.wireOp",EDGE,"E29")])]});
            var sketch = newSketch(context, id + "F40", { "sketchPlane" : qUnion([Q0])});
            skCircle(sketch, "E75", {"center": v(0, 25.4) * mm, "radius": 12.7 * mm});
            skSolve(sketch);
        }
        {
            var Q0;
            Q0 = qSketchRegion(id + "F40", true);
            extrude(context, id + "F41", {"entities" : qUnion([Q0]), "operationType" : NewBodyOperationType.ADD, "depth" : 25.4 * mm, "offsetDistance" : 25.4 * mm});
        }
        {
            var Q0;
            Q0=makeQuery(id+"F15.opExtrude","SWEPT_FACE",FACE,{"disambiguationData":[OSD([sQuery(id+"F14.wireOp",EDGE,"E36.top")])]});
            var sketch = newSketch(context, id + "F42", { "sketchPlane" : qUnion([Q0])});
            skCircle(sketch, "E76", {"center": v(104.77, -25.4) * mm, "radius": 22.23 * mm});
            skSolve(sketch);
        }
        {
            var Q0;
            Q0 = qSketchRegion(id + "F42", true);
            var Q1;
            Q1=makeQuery(id+"F3.boolean.opBoolean","COPY",FACE,{"derivedFrom":makeQuery(id+"F3.opExtrude","SWEPT_FACE",FACE,{"disambiguationData":[OSD([sQuery(id+"F2.wireOp",EDGE,"E20")])]})});
            extrude(context, id + "F43", {"entities" : qUnion([Q0]), "endBound" : BoundingType.UP_TO_SURFACE, "depth" : 6.35 * mm, "endBoundEntityFace" : qUnion([Q1]), "offsetDistance" : 25.4 * mm});
        }
        {
            var Q0;
            Q0=makeQuery(id+"F43.opExtrude","SWEPT_BODY",BODY,{"disambiguationData":[OSD([sQuery(id+"F42.wireOp",EDGE,"E76")])]});
            var Q1;
            Q1=qCreatedBy(id+"F7.planeOp",FACE);
            mirror(context, id + "F44", {"operationType" : NewBodyOperationType.ADD, "entities" : qUnion([Q0]), "mirrorPlane" : qUnion([Q1])});
        }
    });
